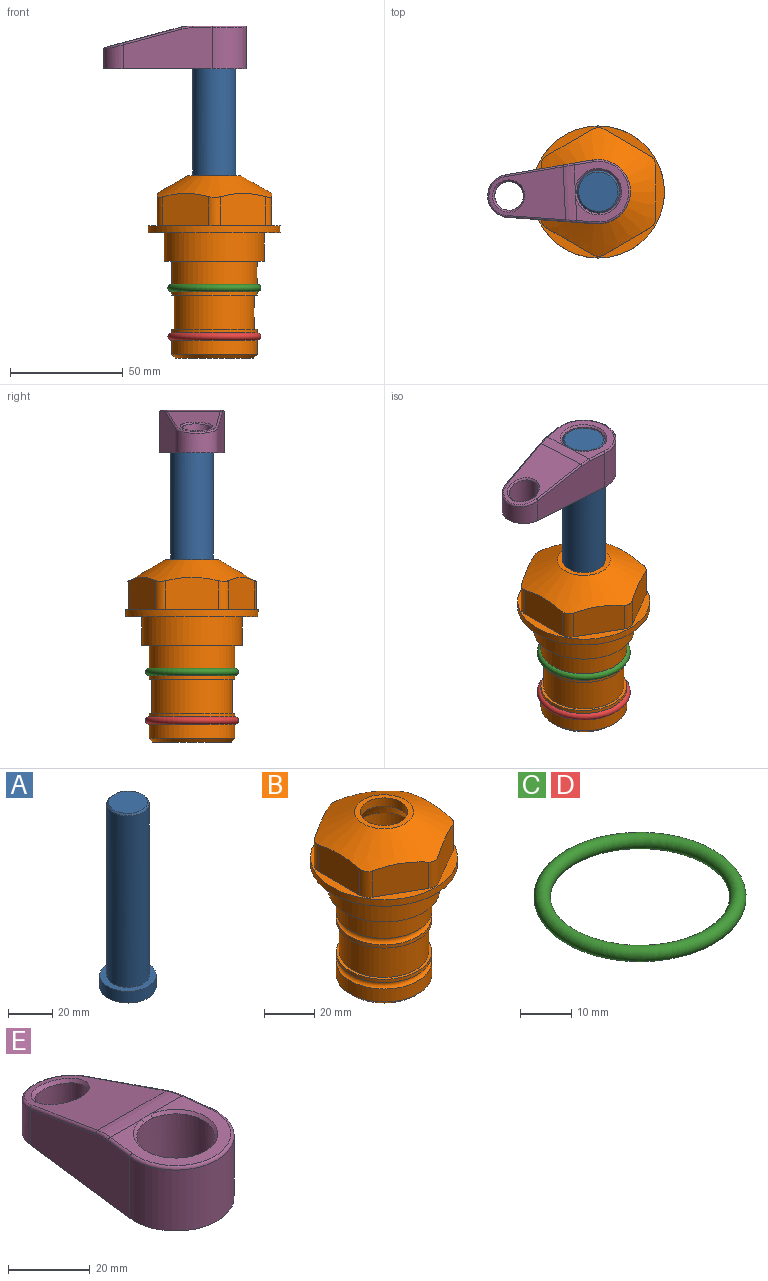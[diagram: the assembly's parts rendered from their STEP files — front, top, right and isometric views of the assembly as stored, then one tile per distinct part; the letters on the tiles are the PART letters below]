
ASSEMBLY  parts=5 mates=4
PART A: 6 faces, bbox 25.4x25.4x101.6 mm
  f0: plane 17.46x17.46mm, normal (0,0,1), area 239.5mm2, adj f5
  f1: plane 25.4x25.4mm, normal (0,0,-1), area 506.7mm2, adj f2
  f2: cylinder r=12.7mm len=25.4mm, axis (0,0,1), area 506.7mm2, adj f1,f3
  f3: plane 25.4x25.4mm, normal (0,0,1), area 221.7mm2, adj f2,f4
  f4: cylinder r=9.53mm len=94.46mm, axis (0,0,1), area 5653mm2, adj f3,f5
  f5: cone r=8.73mm half-angle=45deg, axis (0,0,-1), area 64.4mm2, adj f0,f4
PART B: 36 faces, bbox 58.7x58.7x81 mm
  f0: cylinder r=17.78mm len=35.56mm, axis (0,0,1), area 1670.8mm2, adj f23,f24,f31
  f1: cylinder r=19.05mm len=38.1mm, axis (0,0,1), area 1191.9mm2, adj f26,f27,f30
  f2: plane 58.66x58.66mm, normal (0,0,-1), area 1150.6mm2, adj f3,f28
  f3: cylinder r=29.33mm len=58.66mm, axis (0,0,-1), area 585.1mm2, adj f2,f4
  f4: plane 58.66x58.66mm, normal (0,0,1), area 475.9mm2, adj f3,f5,f6,f7,f8,f9,f10,f11
  f5: plane 20.32x14.34mm, normal (-0.5,0.87,0), area 324.4mm2, adj f4,f15,f16,f17
  f6: plane 20.32x14.34mm, normal (0.5,0.87,0), area 324.4mm2, adj f4,f14,f15,f17
  f7: plane 23.48x14.34mm, normal (1,0,0), area 324.4mm2, adj f4,f13,f14,f17
  f8: plane 20.32x14.34mm, normal (0.5,-0.87,0), area 324.4mm2, adj f4,f12,f13,f17
  f9: plane 20.32x14.34mm, normal (-0.5,-0.87,0), area 324.4mm2, adj f4,f11,f12,f17
  f10: plane 23.48x14.34mm, normal (-1,0,0), area 324.4mm2, adj f4,f11,f16,f17
  f11: cylinder r=5.08mm len=12.85mm, axis (0,0,-1), area 67.2mm2, adj f4,f9,f10,f17
  f12: cylinder r=5.08mm len=12.85mm, axis (0,0,-1), area 67.2mm2, adj f4,f8,f9,f17
  f13: cylinder r=5.08mm len=12.85mm, axis (0,0,-1), area 67.2mm2, adj f4,f7,f8,f17
  f14: cylinder r=5.08mm len=12.85mm, axis (0,0,-1), area 67.2mm2, adj f4,f6,f7,f17
  f15: cylinder r=5.08mm len=12.85mm, axis (0,0,-1), area 67.2mm2, adj f4,f5,f6,f17
  f16: cylinder r=5.08mm len=12.85mm, axis (0,0,-1), area 67.2mm2, adj f4,f5,f10,f17
  f17: cone r=11.73mm half-angle=60deg, axis (0,0,-1), area 2071.8mm2, adj f5,f6,f7,f8,f9,f10,f11,f12
  f18: plane 23.46x23.46mm, normal (0,0,1), area 147.4mm2, adj f17,f35
  f19: plane 34.93x34.93mm, normal (0,0,-1), area 958mm2, adj f29
  f20: cylinder r=19.05mm len=38.1mm, axis (0,0,1), area 760.1mm2, adj f21,f29
  f21: torus R=19.05mm, axis (0,0,1), area 565.3mm2, adj f20,f22
  f22: cylinder r=19.05mm len=38.1mm, axis (0,0,1), area 190mm2, adj f21,f23
  f23: plane 38.1x38.1mm, normal (0,0,1), area 146.9mm2, adj f0,f22
  f24: plane 38.1x38.1mm, normal (0,0,-1), area 146.9mm2, adj f0,f25
  f25: cylinder r=19.05mm len=38.1mm, axis (0,0,1), area 190mm2, adj f24,f26
  f26: torus R=19.05mm, axis (0,0,1), area 565.3mm2, adj f1,f25
  f27: plane 44.45x44.45mm, normal (0,0,-1), area 411.7mm2, adj f1,f28
  f28: cylinder r=22.23mm len=44.45mm, axis (0,0,1), area 1773.5mm2, adj f2,f27
  f29: cone r=19.05mm half-angle=45deg, axis (0,0,1), area 257.5mm2, adj f19,f20
  f30: cylinder r=3.17mm len=6.75mm, axis (-1,0,0), area 128mm2, adj f1,f33
  f31: cylinder r=3.17mm len=6.35mm, axis (-1,0,0), area 102.5mm2, adj f0,f33
  f32: plane 25.4x25.4mm, normal (0,0,1), area 506.7mm2, adj f33
  f33: cylinder r=12.7mm len=66.42mm, axis (0,0,-1), area 5236.2mm2, adj f30,f31,f32,f34
  f34: cone r=9.53mm half-angle=30deg, axis (0,0,-1), area 443.4mm2, adj f33,f35
  f35: cylinder r=9.53mm len=19.05mm, axis (0,0,-1), area 240.9mm2, adj f18,f34
PART C: 1 faces, bbox 44.7x44.7x3.2 mm
  f0: torus R=19.05mm, axis (0,0,1), area 1193.9mm2
PART D: same geometry as C
PART E: 31 faces, bbox 31.7x65.5x19.8 mm
  f0: plane 39.12x18.26mm, normal (0.99,0.12,0), area 612.2mm2, adj f1,f4,f7,f11,f13,f15
  f1: cylinder r=9.53mm len=18.91mm, axis (0,0,-1), area 296.1mm2, adj f0,f2,f7,f17
  f2: plane 39.12x18.26mm, normal (-0.99,0.12,0), area 612.2mm2, adj f1,f4,f7,f12,f14,f16
  f3: cylinder r=6.35mm len=12.7mm, axis (0,0,-1), area 362.4mm2, adj f7,f18
  f4: cylinder r=14.29mm len=28.58mm, axis (0,0,-1), area 882.2mm2, adj f0,f2,f7,f10
  f5: cylinder r=9.53mm len=19.05mm, axis (0,0,-1), area 1092.6mm2, adj f7,f19,f20
  f6: plane 26.99x23.69mm, normal (0,0,1), area 216.2mm2, adj f9,f10,f11,f12,f19
  f7: plane 63.5x28.58mm, normal (0,0,-1), area 661.8mm2, adj f0,f1,f2,f3,f4,f5,f22,f23
  f8: plane 33.52x23.6mm, normal (0,0.26,0.97), area 486mm2, adj f9,f15,f16,f17,f18
  f9: cylinder r=19.05mm len=24.72mm, axis (1,0,0), area 120.4mm2, adj f6,f8,f13,f14,f20
  f10: torus R=13.49mm, axis (0,0,1), area 59mm2, adj f4,f6,f11,f12
  f11: cylinder r=0.79mm len=8.67mm, axis (0.12,-0.99,0), area 10.8mm2, adj f0,f6,f10,f13
  f12: cylinder r=0.79mm len=8.67mm, axis (0.12,0.99,0), area 10.8mm2, adj f2,f6,f10,f14
  f13: bspline ~4.95x1.42mm, area 6.1mm2, adj f0,f9,f11,f15
  f14: bspline ~4.95x1.42mm, area 6.1mm2, adj f2,f9,f12,f16
  f15: cylinder r=0.79mm len=25.95mm, axis (0.12,-0.96,0.26), area 32.9mm2, adj f0,f8,f13,f17
  f16: cylinder r=0.79mm len=25.95mm, axis (0.12,0.96,-0.26), area 32.9mm2, adj f2,f8,f14,f17
  f17: bspline ~18.91x8.38mm, area 30mm2, adj f1,f8,f15,f16
  f18: bspline ~14.29x14.29mm, area 48.3mm2, adj f3,f8
  f19: cone r=9.53mm half-angle=45deg, axis (0,0,1), area 66.5mm2, adj f5,f6,f20
  f20: bspline ~3.22x0.96mm, area 3.5mm2, adj f5,f9,f19
  f21: plane 2.75x2.72mm, normal (0,0,-1), area 2.9mm2, adj f23,f25,f28
  f22: plane 23.05x15.88mm, normal (-0.99,-0.12,0), area 323.6mm2, adj f7,f25,f26,f27,f28,f29
  f23: plane 23.05x15.88mm, normal (0.99,-0.12,0), area 323.6mm2, adj f7,f21,f25,f27,f28,f30
  f24: cylinder r=9.53mm len=10.69mm, axis (0,0,-1), area 114.7mm2, adj f7,f27,f29,f30
  f25: cylinder r=12.7mm len=20.59mm, axis (0,0,-1), area 381.1mm2, adj f7,f21,f22,f23,f26,f28
  f26: plane 2.75x2.72mm, normal (0,0,-1), area 2.9mm2, adj f22,f25,f28
  f27: plane 19.72x18.37mm, normal (0,-0.26,-0.97), area 291.8mm2, adj f22,f23,f24,f28,f29,f30
  f28: cylinder r=15.88mm len=19.92mm, axis (1,0,0), area 54.8mm2, adj f21,f22,f23,f25,f26,f27
  f29: cylinder r=1.59mm len=11mm, axis (0,0,-1), area 34.7mm2, adj f7,f22,f24,f27
  f30: cylinder r=1.59mm len=11mm, axis (0,0,-1), area 34.7mm2, adj f7,f23,f24,f27
PLACE A rot(axis=(0,0,1),92.7deg) t=(0,0,27.55)mm
PLACE B at identity fixed
PLACE C at identity
PLACE D t=(0,0,-21.59)mm
PLACE E rot(axis=(0,0,1),92.7deg) t=(0,0,28.35)mm
MATE fastened A.f2 <-> E.f4  axis (0,0,1) through (0,0,91.05)mm
MATE cylindrical A.f2 <-> B.f0  axis (0,0,-1) through (0,0,-10.55)mm
MATE fastened D.f0 <-> B.f0  axis (0,0,1) through (0,0,-46.1)mm
MATE fastened C.f0 <-> B.f0  axis (0,0,1) through (0,0,-24.51)mm
